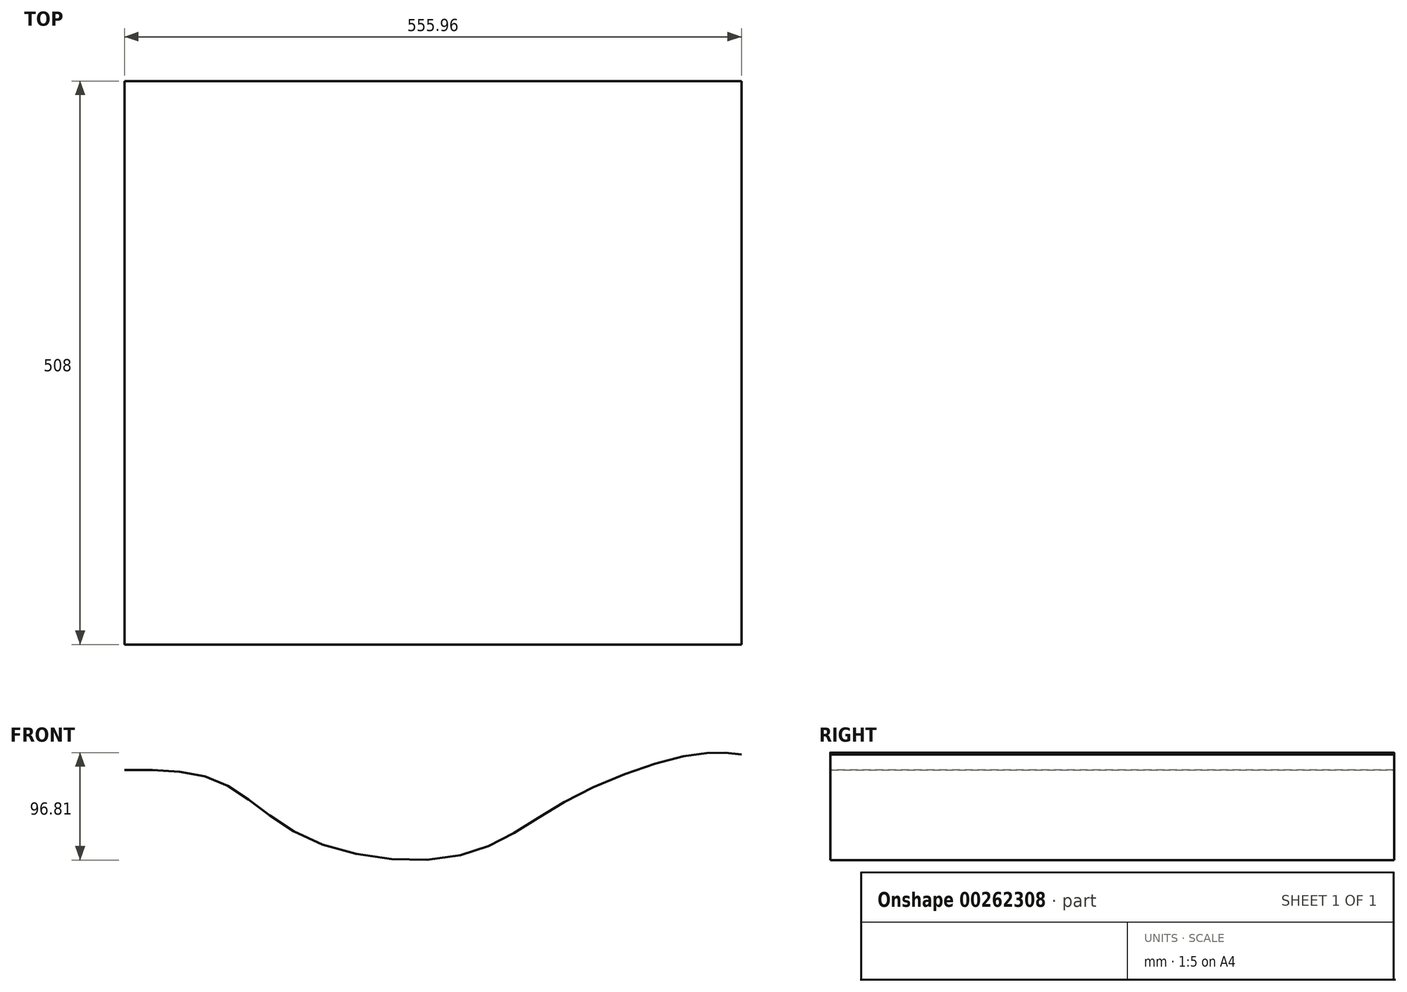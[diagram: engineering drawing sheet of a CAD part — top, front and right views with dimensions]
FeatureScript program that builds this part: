
annotation { "Feature Type Name" : "Feature", "Feature Type Description" : "" }
export const myFeature = defineFeature(function(context is Context, id is Id, definition is map)
    precondition{}
    {
        {
            var Q0;
            Q0=qCreatedBy(makeId("Front.planeOp"),FACE);
            var sketch = newSketch(context, id + "F0", { "sketchPlane" : qUnion([Q0])});
            skFitSpline(sketch, "E0", {"points": [v(-285.72, 333.95) * mm, v(-199.52, 323.17) * mm, v(-124.1, 273.61) * mm, v(19.2, 257.45) * mm, v(114, 307.01) * mm, v(228.22, 347.95) * mm, v(270.24, 347.95) * mm], "startDerivative": vector(581.26, 2.86) * mm, "endDerivative": vector(326.83, -36.86) * mm});
            skSolve(sketch);
        }
        {
            var Q0;
            Q0=sQuery(id+"F0.wireOp",EDGE,"E0");
            extrude(context, id + "F1", {"bodyType" : ToolBodyType.SURFACE, "surfaceEntities" : qUnion([Q0]), "endBound" : BoundingType.SYMMETRIC, "depth" : 508 * mm});
        }
    });
